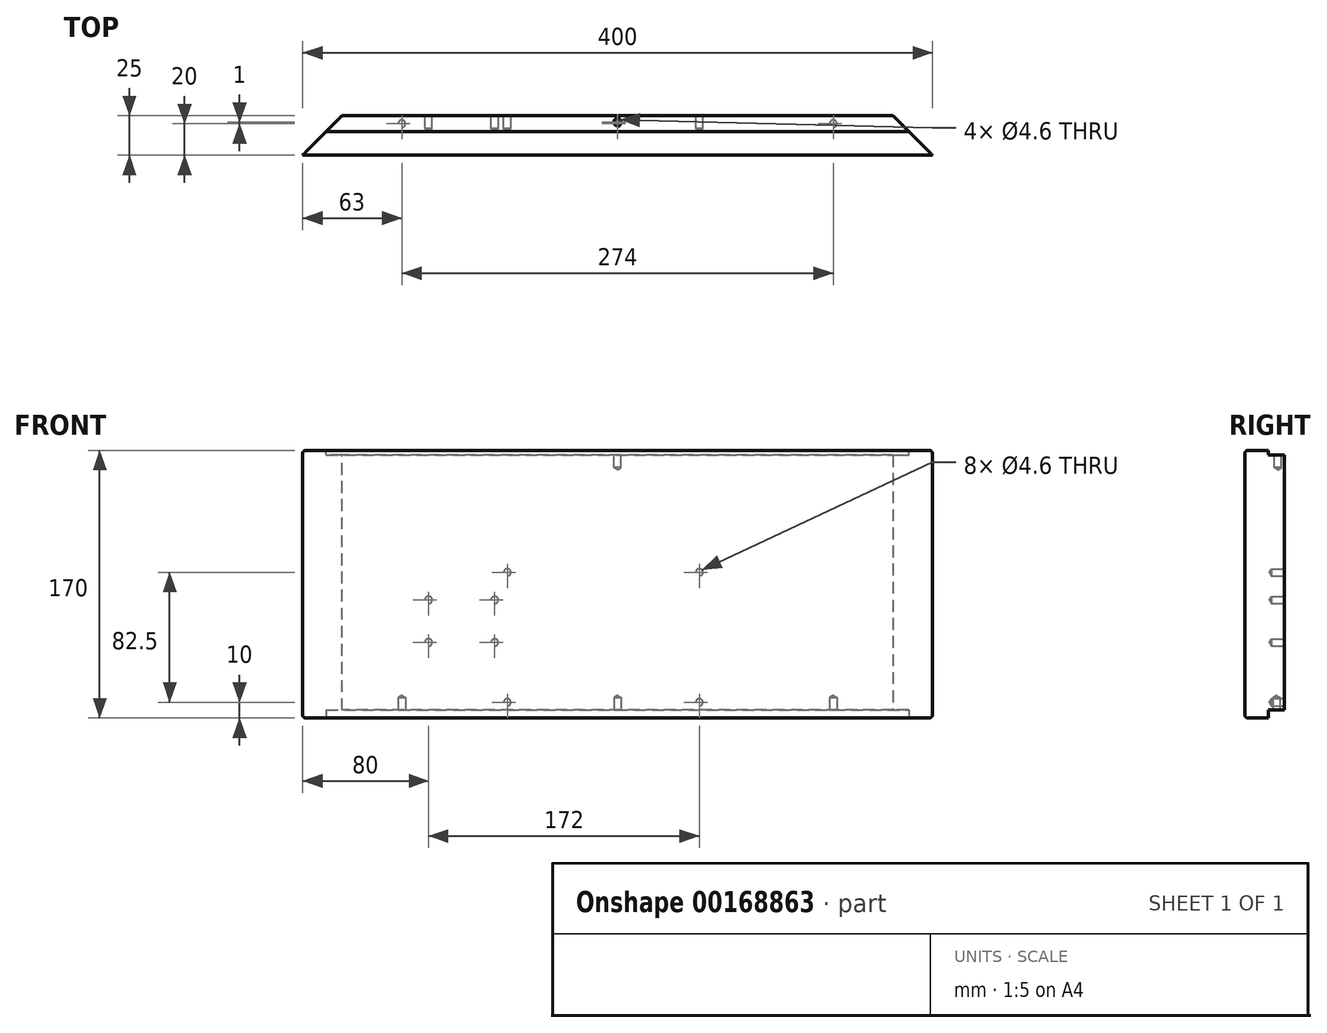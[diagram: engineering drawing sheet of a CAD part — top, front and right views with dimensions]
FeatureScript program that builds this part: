
annotation { "Feature Type Name" : "Feature", "Feature Type Description" : "" }
export const myFeature = defineFeature(function(context is Context, id is Id, definition is map)
    precondition{}
    {
        {
            var Q0;
            Q0=qCreatedBy(makeId("Front.planeOp"),FACE);
            var sketch = newSketch(context, id + "F0", { "sketchPlane" : qUnion([Q0])});
            skLineSegment(sketch, "E0.bottom", {"start": v(200, -85) * mm, "end": v(-200, -85) * mm});
            skLineSegment(sketch, "E0.top", {"start": v(200, 85) * mm, "end": v(-200, 85) * mm});
            skLineSegment(sketch, "E0.left", {"start": v(200, -85) * mm, "end": v(200, 85) * mm});
            skLineSegment(sketch, "E0.right", {"start": v(-200, -85) * mm, "end": v(-200, 85) * mm});
            skPoint(sketch, "E0.middle", {"position": v(0, 0) * mm});
            skSolve(sketch);
        }
        {
            var Q0;
            Q0=makeQuery(id+"F0.imprint","IMPRINT",FACE,{"disambiguationData":[TD([[makeQuery(id+"F0.imprint","IMPRINT",EDGE,{"derivedFrom":sQuery(id+"F0.wireOp",EDGE,"E0.bottom")}),-1.0]])]});
            extrude(context, id + "F1", {"entities" : qUnion([Q0]), "depth" : 25 * mm});
        }
        {
            var Q0;
            Q0=makeQuery(id+"F1.opExtrude","CAP_EDGE",EDGE,{"disambiguationData":[OSD([sQuery(id+"F0.wireOp",EDGE,"E0.right")])],"isStart":true});
            var Q1;
            Q1=makeQuery(id+"F1.opExtrude","CAP_EDGE",EDGE,{"disambiguationData":[OSD([sQuery(id+"F0.wireOp",EDGE,"E0.left")])],"isStart":true});
            chamfer(context, id + "F2", {"entities" : qUnion([Q0, Q1]), "width" : 25 * mm, "tangentPropagation" : true});
        }
        {
            var Q0;
            Q0=makeQuery(id+"F1.opExtrude","SWEPT_FACE",FACE,{"disambiguationData":[OSD([sQuery(id+"F0.wireOp",EDGE,"E0.top")])]});
            var sketch = newSketch(context, id + "F3", { "sketchPlane" : qUnion([Q0])});
            skLineSegment(sketch, "E1", {"start": v(-185, -10) * mm, "end": v(185, -10) * mm});
            skSolve(sketch);
        }
        {
            var Q0;
            {var subQ0=sQuery(id+"F3.wireOp",EDGE,"E1");Q0=makeQuery(id+"F3.imprint","IMPRINT",FACE,{"disambiguationData":[TD([[makeQuery(id+"F3.imprint","IMPRINT",EDGE,{"derivedFrom":subQ0}),1.0]])]});}
            extrude(context, id + "F4", {"entities" : qUnion([Q0]), "operationType" : NewBodyOperationType.REMOVE, "oppositeDirection" : true, "depth" : 3 * mm});
        }
        {
            var Q0;
            Q0=makeQuery(id+"F1.opExtrude","SWEPT_FACE",FACE,{"disambiguationData":[OSD([sQuery(id+"F0.wireOp",EDGE,"E0.bottom")])]});
            var sketch = newSketch(context, id + "F5", { "sketchPlane" : qUnion([Q0])});
            skLineSegment(sketch, "E2", {"start": v(-185, 10) * mm, "end": v(185, 10) * mm});
            skSolve(sketch);
        }
        {
            var Q0;
            {var subQ0=sQuery(id+"F5.wireOp",EDGE,"E2");Q0=makeQuery(id+"F5.imprint","IMPRINT",FACE,{"disambiguationData":[TD([[makeQuery(id+"F5.imprint","IMPRINT",EDGE,{"derivedFrom":subQ0}),-1.0]])]});}
            extrude(context, id + "F6", {"entities" : qUnion([Q0]), "operationType" : NewBodyOperationType.REMOVE, "oppositeDirection" : true, "depth" : 5 * mm});
        }
        {
            var Q0;
            Q0=makeQuery(id+"F0.imprint","IMPRINT",FACE,{"disambiguationData":[TD([[makeQuery(id+"F0.imprint","IMPRINT",EDGE,{"derivedFrom":sQuery(id+"F0.wireOp",EDGE,"E0.bottom")}),-1.0]])]});
            var sketch = newSketch(context, id + "F7", { "sketchPlane" : qUnion([Q0])});
            skLineSegment(sketch, "E3", {"start": v(127.78, 7.5) * mm, "end": v(-146.68, 7.5) * mm, "construction": true});
            skLineSegment(sketch, "E4", {"start": v(-14.15, -10) * mm, "end": v(-150.88, -10) * mm, "construction": true});
            skLineSegment(sketch, "E5", {"start": v(127.98, -75) * mm, "end": v(-156.49, -75) * mm, "construction": true});
            skLineSegment(sketch, "E6", {"start": v(-14.55, -37) * mm, "end": v(-153.09, -37) * mm, "construction": true});
            skLineSegment(sketch, "E7", {"start": v(-120, 39.85) * mm, "end": v(-120, -25.61) * mm, "construction": true});
            skLineSegment(sketch, "E8", {"start": v(-78, 39.45) * mm, "end": v(-78, -25.01) * mm, "construction": true});
            skLineSegment(sketch, "E9", {"start": v(-70, 52.46) * mm, "end": v(-70, -53.37) * mm, "construction": true});
            skLineSegment(sketch, "E10", {"start": v(52, 50.66) * mm, "end": v(52, -53.37) * mm, "construction": true});
            skPoint(sketch, "E11", {"position": v(52, 7.5) * mm});
            skPoint(sketch, "E12", {"position": v(-70, 7.5) * mm});
            skPoint(sketch, "E13", {"position": v(-78, -10) * mm});
            skPoint(sketch, "E14", {"position": v(-120, -10) * mm});
            skPoint(sketch, "E15", {"position": v(-120, -37) * mm});
            skPoint(sketch, "E16", {"position": v(-78, -37) * mm});
            skPoint(sketch, "E17", {"position": v(52, -75) * mm});
            skPoint(sketch, "E18", {"position": v(-70, -75) * mm});
            skSolve(sketch);
        }
        {
            var Q0;
            Q0=sQuery(id+"F7.wireOp",VERTEX,"E11");
            var Q1;
            Q1=sQuery(id+"F7.wireOp",VERTEX,"E12");
            var Q2;
            Q2=sQuery(id+"F7.wireOp",VERTEX,"E14");
            var Q3;
            Q3=sQuery(id+"F7.wireOp",VERTEX,"E13");
            var Q4;
            Q4=sQuery(id+"F7.wireOp",VERTEX,"E16");
            var Q5;
            Q5=sQuery(id+"F7.wireOp",VERTEX,"E15");
            var Q6;
            Q6=sQuery(id+"F7.wireOp",VERTEX,"E18");
            var Q7;
            Q7=sQuery(id+"F7.wireOp",VERTEX,"E17");
            var Q8;
            Q8=makeQuery(id+"F1.opExtrude","SWEPT_BODY",BODY,{"disambiguationData":[OSD([sQuery(id+"F0.wireOp",EDGE,"E0.bottom"),sQuery(id+"F0.wireOp",EDGE,"E0.top"),sQuery(id+"F0.wireOp",EDGE,"E0.left"),sQuery(id+"F0.wireOp",EDGE,"E0.right")])]});
            hole(context, id + "F8", {"style" : HoleStyle.SIMPLE, "endStyle" : HoleEndStyle.BLIND, "oppositeDirection" : true, "holeDiameter" : 4.6 * mm, "holeDepth" : 8 * mm, "startFromSketch" : true, "locations" : qUnion([Q0, Q1, Q2, Q3, Q4, Q5, Q6, Q7]), "scope" : qUnion([Q8])});
        }
        {
            var Q0;
            Q0=makeQuery(id+"F4.boolean.opBoolean","COPY",FACE,{"derivedFrom":makeQuery(id+"F4.opExtrude","CAP_FACE",FACE,{"disambiguationData":[OSD([sQuery(id+"F0.wireOp",EDGE,"E0.top"),sQuery(id+"F0.wireOp",EDGE,"E0.left"),sQuery(id+"F0.wireOp",EDGE,"E0.right"),sQuery(id+"F3.wireOp",EDGE,"E1")])],"isStart":false})});
            var sketch = newSketch(context, id + "F9", { "sketchPlane" : qUnion([Q0])});
            skLineSegment(sketch, "E19", {"start": v(-168.3, -4) * mm, "end": v(166.3, -4) * mm, "construction": true});
            skLineSegment(sketch, "E20", {"start": v(0, 10.85) * mm, "end": v(0, -15.9) * mm, "construction": true});
            skPoint(sketch, "E20.endSnap0", {"position": v(0, -10) * mm});
            skPoint(sketch, "E21", {"position": v(0, -4) * mm});
            skSolve(sketch);
        }
        {
            var Q0;
            Q0=sQuery(id+"F9.wireOp",VERTEX,"E21");
            var Q1;
            Q1=makeQuery(id+"F1.opExtrude","SWEPT_BODY",BODY,{"disambiguationData":[OSD([sQuery(id+"F0.wireOp",EDGE,"E0.bottom"),sQuery(id+"F0.wireOp",EDGE,"E0.top"),sQuery(id+"F0.wireOp",EDGE,"E0.left"),sQuery(id+"F0.wireOp",EDGE,"E0.right")])]});
            hole(context, id + "F10", {"style" : HoleStyle.SIMPLE, "endStyle" : HoleEndStyle.BLIND, "holeDiameter" : 4.6 * mm, "holeDepth" : 8 * mm, "startFromSketch" : true, "locations" : qUnion([Q0]), "scope" : qUnion([Q1])});
        }
        {
            var Q0;
            Q0=makeQuery(id+"F6.boolean.opBoolean","COPY",FACE,{"derivedFrom":makeQuery(id+"F6.opExtrude","CAP_FACE",FACE,{"disambiguationData":[OSD([sQuery(id+"F0.wireOp",EDGE,"E0.bottom"),sQuery(id+"F0.wireOp",EDGE,"E0.left"),sQuery(id+"F0.wireOp",EDGE,"E0.right"),sQuery(id+"F5.wireOp",EDGE,"E2")])],"isStart":false})});
            var sketch = newSketch(context, id + "F11", { "sketchPlane" : qUnion([Q0])});
            skLineSegment(sketch, "E22", {"start": v(-222.57, 5) * mm, "end": v(216.71, 5) * mm, "construction": true});
            skLineSegment(sketch, "E23", {"start": v(-137, 28.3) * mm, "end": v(-137, -15.54) * mm, "construction": true});
            skLineSegment(sketch, "E24", {"start": v(137, 29.01) * mm, "end": v(137, -22.56) * mm, "construction": true});
            skLineSegment(sketch, "E25", {"start": v(0, 22.52) * mm, "end": v(0, -13.9) * mm, "construction": true});
            skPoint(sketch, "E26", {"position": v(-137, 5) * mm});
            skPoint(sketch, "E27", {"position": v(137, 5) * mm});
            skPoint(sketch, "E28", {"position": v(0, 5) * mm});
            skSolve(sketch);
        }
        {
            var Q0;
            Q0=sQuery(id+"F11.wireOp",VERTEX,"E26");
            var Q1;
            Q1=sQuery(id+"F11.wireOp",VERTEX,"E28");
            var Q2;
            Q2=sQuery(id+"F11.wireOp",VERTEX,"E27");
            var Q3;
            Q3=makeQuery(id+"F1.opExtrude","SWEPT_BODY",BODY,{"disambiguationData":[OSD([sQuery(id+"F0.wireOp",EDGE,"E0.bottom"),sQuery(id+"F0.wireOp",EDGE,"E0.top"),sQuery(id+"F0.wireOp",EDGE,"E0.left"),sQuery(id+"F0.wireOp",EDGE,"E0.right")])]});
            hole(context, id + "F12", {"style" : HoleStyle.SIMPLE, "endStyle" : HoleEndStyle.BLIND, "holeDiameter" : 4.6 * mm, "holeDepth" : 8 * mm, "startFromSketch" : true, "locations" : qUnion([Q0, Q1, Q2]), "scope" : qUnion([Q3])});
        }
        {
            var Q0;
            Q0=makeQuery(id+"F1.opExtrude","CAP_EDGE",EDGE,{"disambiguationData":[OSD([sQuery(id+"F0.wireOp",EDGE,"E0.top")])],"isStart":false});
            var Q1;
            Q1=makeQuery(id+"F1.opExtrude","CAP_EDGE",EDGE,{"disambiguationData":[OSD([sQuery(id+"F0.wireOp",EDGE,"E0.bottom")])],"isStart":false});
            fillet(context, id + "F13", {"entities" : qUnion([Q0, Q1]), "radius" : 2 * mm, "tangentPropagation" : true, "allowEdgeOverflow" : false});
        }
    });
